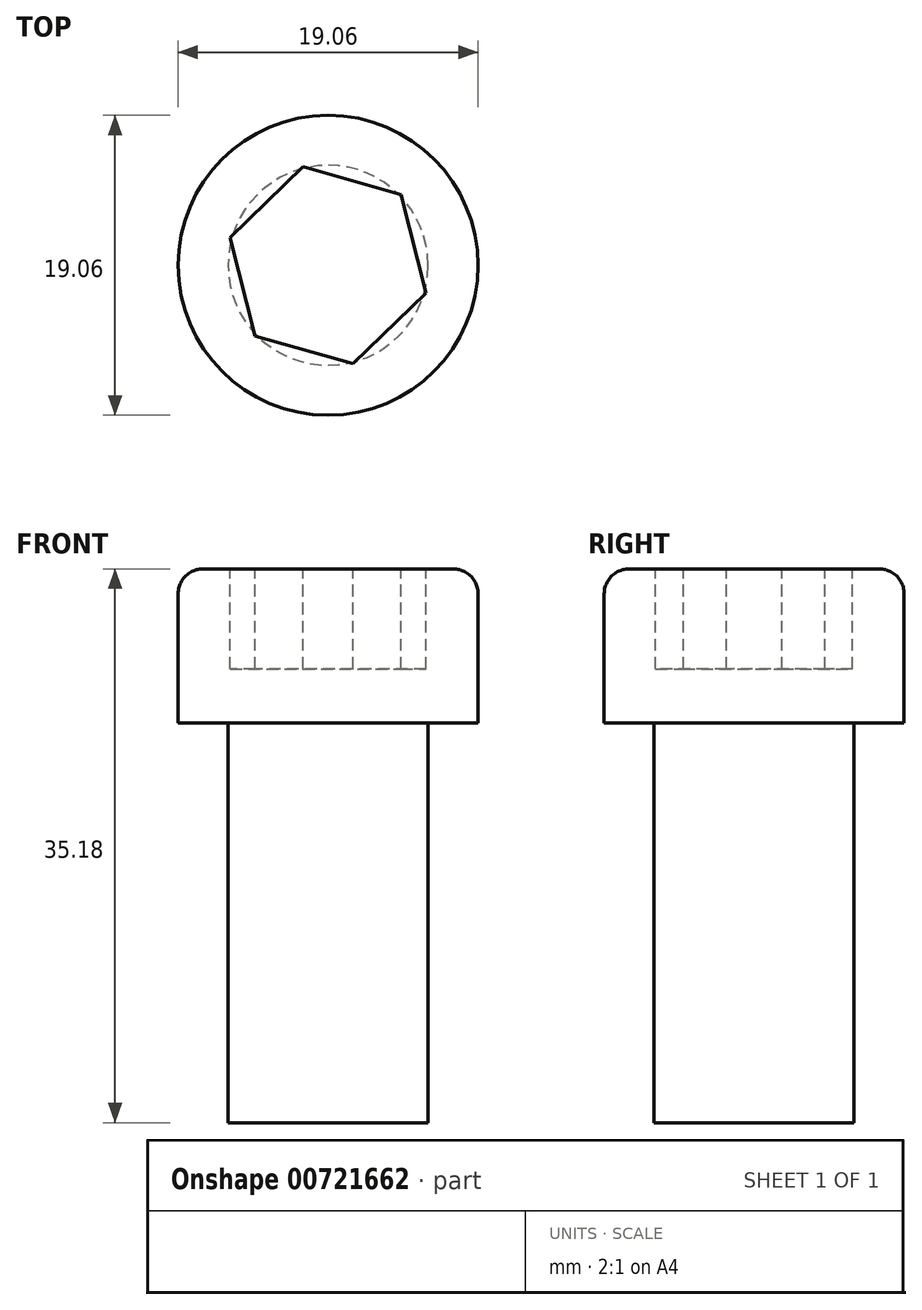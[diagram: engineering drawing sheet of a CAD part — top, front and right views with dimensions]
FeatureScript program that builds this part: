
annotation { "Feature Type Name" : "Feature", "Feature Type Description" : "" }
export const myFeature = defineFeature(function(context is Context, id is Id, definition is map)
    precondition{}
    {
        {
            var Q0;
            Q0=qCreatedBy(makeId("Top.planeOp"),FACE);
            var sketch = newSketch(context, id + "F0", { "sketchPlane" : qUnion([Q0])});
            skCircle(sketch, "E0", {"center": v(0, 0) * mm, "radius": 6.35 * mm});
            skSolve(sketch);
        }
        {
            var Q0;
            Q0 = qSketchRegion(id + "F0", true);
            extrude(context, id + "F1", {"entities" : qUnion([Q0]), "depth" : 25.4 * mm, "offsetDistance" : 25.4 * mm});
        }
        {
            var Q0;
            Q0=makeQuery(id+"F1.opExtrude","CAP_FACE",FACE,{"disambiguationData":[OSD([sQuery(id+"F0.wireOp",EDGE,"E0")])],"isStart":false});
            var sketch = newSketch(context, id + "F2", { "sketchPlane" : qUnion([Q0])});
            skCircle(sketch, "E1", {"center": v(0, 0) * mm, "radius": 9.53 * mm});
            skSolve(sketch);
        }
        {
            var Q0;
            Q0 = qSketchRegion(id + "F2", true);
            extrude(context, id + "F3", {"entities" : qUnion([Q0]), "depth" : 9.84 * mm, "offsetDistance" : 25.4 * mm});
        }
        {
            var Q0;
            Q0=makeQuery(id+"F3.opExtrude","CAP_EDGE",EDGE,{"disambiguationData":[OSD([sQuery(id+"F2.wireOp",EDGE,"E1")])],"isStart":false});
            fillet(context, id + "F4", {"entities" : qUnion([Q0]), "radius" : 1.59 * mm, "tangentPropagation" : true, "allowEdgeOverflow" : false});
        }
        {
            var Q0;
            Q0=makeQuery(id+"F3.opExtrude","CAP_FACE",FACE,{"disambiguationData":[OSD([sQuery(id+"F2.wireOp",EDGE,"E1")])],"isStart":false});
            var sketch = newSketch(context, id + "F5", { "sketchPlane" : qUnion([Q0])});
            skCircle(sketch, "E2.cCircle", {"center": v(0, 0) * mm, "radius": 6.35 * mm, "construction": true});
            skLineSegment(sketch, "E2.0", {"start": v(4.76, 4.2) * mm, "end": v(6.02, -2.02) * mm});
            skLineSegment(sketch, "E2.1", {"start": v(6.02, -2.02) * mm, "end": v(1.26, -6.22) * mm});
            skLineSegment(sketch, "E2.2", {"start": v(1.26, -6.22) * mm, "end": v(-4.76, -4.2) * mm});
            skLineSegment(sketch, "E2.3", {"start": v(-4.76, -4.2) * mm, "end": v(-6.02, 2.02) * mm});
            skLineSegment(sketch, "E2.4", {"start": v(-6.02, 2.02) * mm, "end": v(-1.26, 6.22) * mm});
            skLineSegment(sketch, "E2.5", {"start": v(-1.26, 6.22) * mm, "end": v(4.76, 4.2) * mm});
            skSolve(sketch);
        }
        {
            var Q0;
            Q0 = qSketchRegion(id + "F5", true);
            extrude(context, id + "F6", {"entities" : qUnion([Q0]), "operationType" : NewBodyOperationType.REMOVE, "oppositeDirection" : true, "depth" : 6.35 * mm, "offsetDistance" : 25.4 * mm});
        }
        {
            var Q0;
            Q0=makeQuery(id+"F3.opExtrude","SWEPT_BODY",BODY,{"disambiguationData":[OSD([sQuery(id+"F2.wireOp",EDGE,"E1")])]});
            deleteBodies(context, id + "F7", {"entities" : qUnion([Q0])});
        }
        {
            var Q0;
            Q0=makeQuery(id+"F1.opExtrude","CAP_FACE",FACE,{"disambiguationData":[OSD([sQuery(id+"F0.wireOp",EDGE,"E0")])],"isStart":false});
            var sketch = newSketch(context, id + "F8", { "sketchPlane" : qUnion([Q0])});
            skCircle(sketch, "E3", {"center": v(0, 0) * mm, "radius": 9.53 * mm});
            skSolve(sketch);
        }
        {
            var Q0;
            Q0 = qSketchRegion(id + "F8", true);
            extrude(context, id + "F9", {"entities" : qUnion([Q0]), "operationType" : NewBodyOperationType.ADD, "depth" : 9.78 * mm, "offsetDistance" : 25.4 * mm});
        }
        {
            var Q0;
            Q0=makeQuery(id+"F9.opExtrude","CAP_EDGE",EDGE,{"disambiguationData":[OSD([sQuery(id+"F8.wireOp",EDGE,"E3")])],"isStart":false});
            fillet(context, id + "F10", {"entities" : qUnion([Q0]), "radius" : 1.59 * mm, "tangentPropagation" : true, "allowEdgeOverflow" : false});
        }
        {
            var Q0;
            Q0=makeQuery(id+"F9.opExtrude","CAP_FACE",FACE,{"disambiguationData":[OSD([sQuery(id+"F8.wireOp",EDGE,"E3")])],"isStart":false});
            var sketch = newSketch(context, id + "F11", { "sketchPlane" : qUnion([Q0])});
            skCircle(sketch, "E4.cCircle", {"center": v(0, 0) * mm, "radius": 5.59 * mm, "construction": true});
            skLineSegment(sketch, "E4.0", {"start": v(6.2, -1.75) * mm, "end": v(1.59, -6.25) * mm});
            skLineSegment(sketch, "E4.1", {"start": v(1.59, -6.25) * mm, "end": v(-4.62, -4.5) * mm});
            skLineSegment(sketch, "E4.2", {"start": v(-4.62, -4.5) * mm, "end": v(-6.2, 1.75) * mm});
            skLineSegment(sketch, "E4.3", {"start": v(-6.2, 1.75) * mm, "end": v(-1.59, 6.25) * mm});
            skLineSegment(sketch, "E4.4", {"start": v(-1.59, 6.25) * mm, "end": v(4.62, 4.5) * mm});
            skLineSegment(sketch, "E4.5", {"start": v(4.62, 4.5) * mm, "end": v(6.2, -1.75) * mm});
            skPoint(sketch, "E4.0.midPoint", {"position": v(3.9, -4) * mm});
            skSolve(sketch);
        }
        {
            var Q0;
            Q0 = qSketchRegion(id + "F11", true);
            extrude(context, id + "F12", {"entities" : qUnion([Q0]), "operationType" : NewBodyOperationType.REMOVE, "oppositeDirection" : true, "depth" : 6.35 * mm, "offsetDistance" : 25.4 * mm});
        }
    });
